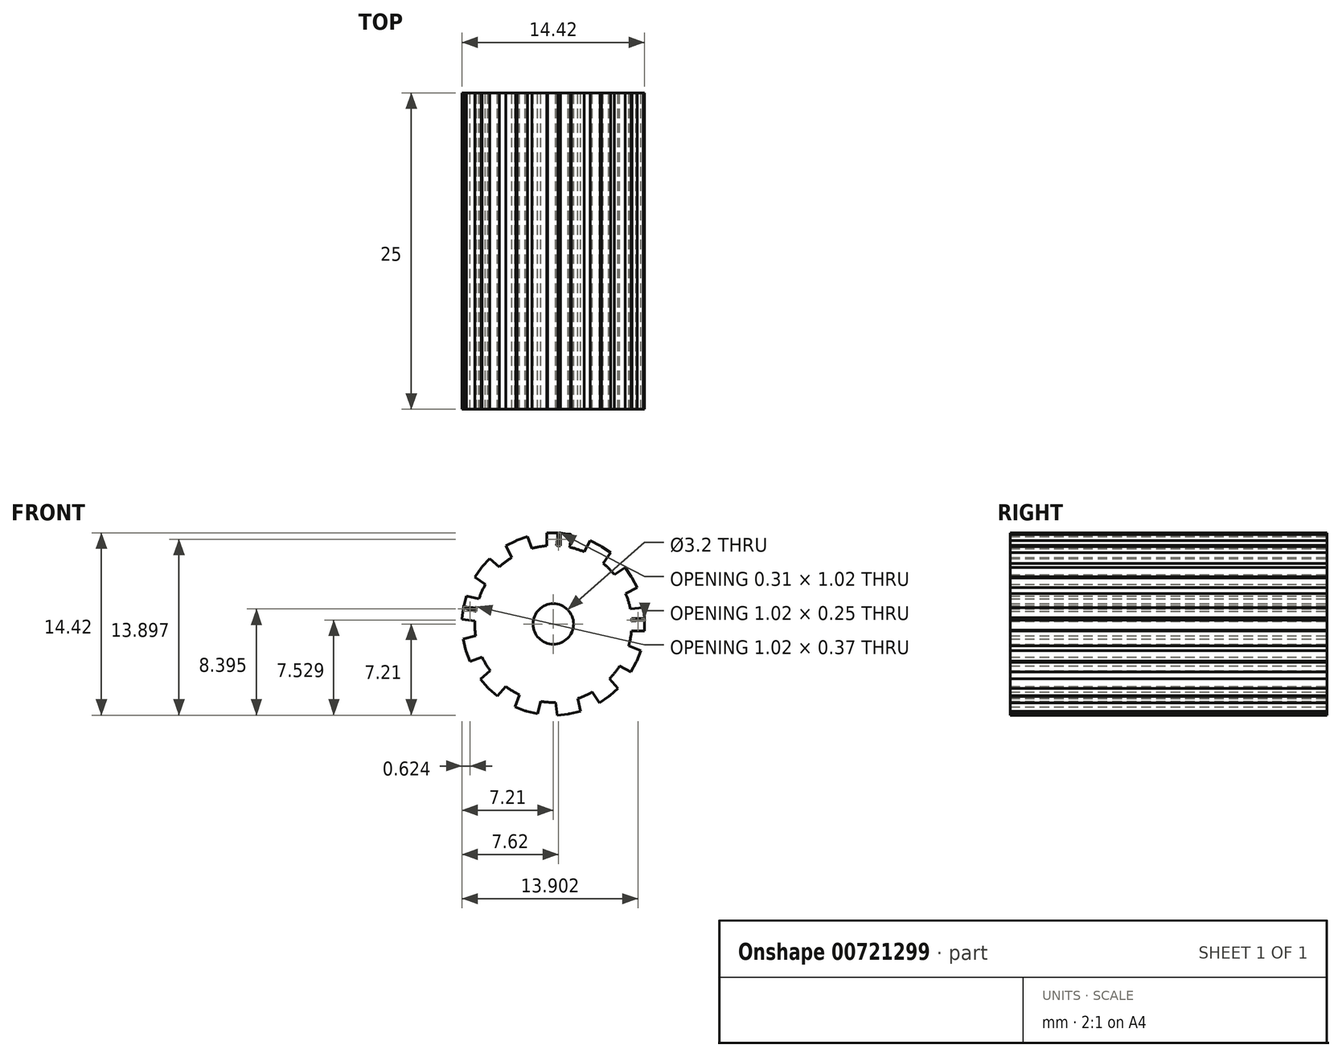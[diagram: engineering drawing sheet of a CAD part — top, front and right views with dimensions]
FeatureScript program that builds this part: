
annotation { "Feature Type Name" : "Feature", "Feature Type Description" : "" }
export const myFeature = defineFeature(function(context is Context, id is Id, definition is map)
    precondition{}
    {
        {
            var Q0;
            Q0=qCreatedBy(makeId("Front.planeOp"),FACE);
            var sketch = newSketch(context, id + "F0", { "sketchPlane" : qUnion([Q0])});
            skCircle(sketch, "E0", {"center": v(0, 0) * mm, "radius": 6.2 * mm});
            skCircle(sketch, "E1", {"center": v(0, 0) * mm, "radius": 4.5 * mm});
            skLineSegment(sketch, "E2", {"start": v(-0.5, 7.2) * mm, "end": v(0.5, 7.2) * mm});
            skLineSegment(sketch, "E3", {"start": v(-0.5, 7.2) * mm, "end": v(-0.5, 6.18) * mm});
            skLineSegment(sketch, "E4", {"start": v(0.5, 7.2) * mm, "end": v(0.5, 6.18) * mm});
            skPoint(sketch, "E5.end.orphan", {"position": v(0, 7.2) * mm});
            skPoint(sketch, "E5.start.orphan", {"position": v(0, 6.2) * mm});
            skLineSegment(sketch, "E6", {"start": v(7.2, 0.5) * mm, "end": v(7.2, -0.5) * mm});
            skLineSegment(sketch, "E7", {"start": v(7.2, 0.5) * mm, "end": v(6.18, 0.5) * mm});
            skLineSegment(sketch, "E8", {"start": v(7.2, -0.5) * mm, "end": v(6.18, -0.5) * mm});
            skPoint(sketch, "E9.end.orphan", {"position": v(7.2, 0) * mm});
            skPoint(sketch, "E9.start.orphan", {"position": v(6.2, 0) * mm});
            skLineSegment(sketch, "E10.1.0", {"start": v(-7.09, 1.37) * mm, "end": v(-6.07, 1.25) * mm});
            skLineSegment(sketch, "E10.1.1", {"start": v(-7.2, 0.38) * mm, "end": v(-6.2, 0.25) * mm});
            skPoint(sketch, "E10.1.2", {"position": v(-7.15, 0.87) * mm});
            skLineSegment(sketch, "E10.1.3", {"start": v(-7.2, 0.38) * mm, "end": v(-7.09, 1.37) * mm});
            skLineSegment(sketch, "E10.1.4", {"start": v(0.38, 7.2) * mm, "end": v(0.25, 6.2) * mm});
            skLineSegment(sketch, "E10.1.5", {"start": v(1.37, 7.09) * mm, "end": v(1.25, 6.07) * mm});
            skLineSegment(sketch, "E10.1.6", {"start": v(0.38, 7.2) * mm, "end": v(1.37, 7.09) * mm});
            skLineSegment(sketch, "E10.2.0", {"start": v(-2.22, -6.87) * mm, "end": v(-1.97, -5.88) * mm});
            skLineSegment(sketch, "E10.2.1", {"start": v(-1.25, -7.1) * mm, "end": v(-1, -6.12) * mm});
            skPoint(sketch, "E10.2.2", {"position": v(-1.73, -6.99) * mm});
            skLineSegment(sketch, "E10.2.3", {"start": v(-1.25, -7.1) * mm, "end": v(-2.22, -6.87) * mm});
            skLineSegment(sketch, "E10.2.4", {"start": v(-7.1, 1.25) * mm, "end": v(-6.12, 1) * mm});
            skLineSegment(sketch, "E10.2.5", {"start": v(-6.87, 2.22) * mm, "end": v(-5.88, 1.97) * mm});
            skLineSegment(sketch, "E10.2.6", {"start": v(-7.1, 1.25) * mm, "end": v(-6.87, 2.22) * mm});
            skLineSegment(sketch, "E10.3.0", {"start": v(6.55, -3.03) * mm, "end": v(5.6, -2.67) * mm});
            skLineSegment(sketch, "E10.3.1", {"start": v(6.9, -2.1) * mm, "end": v(5.95, -1.74) * mm});
            skPoint(sketch, "E10.3.2", {"position": v(6.73, -2.57) * mm});
            skLineSegment(sketch, "E10.3.3", {"start": v(6.9, -2.1) * mm, "end": v(6.55, -3.03) * mm});
            skLineSegment(sketch, "E10.3.4", {"start": v(-2.1, -6.9) * mm, "end": v(-1.74, -5.95) * mm});
            skLineSegment(sketch, "E10.3.5", {"start": v(-3.03, -6.55) * mm, "end": v(-2.67, -5.6) * mm});
            skLineSegment(sketch, "E10.3.6", {"start": v(-2.1, -6.9) * mm, "end": v(-3.03, -6.55) * mm});
            skLineSegment(sketch, "E10.4.0", {"start": v(3.8, 6.13) * mm, "end": v(3.33, 5.23) * mm});
            skLineSegment(sketch, "E10.4.1", {"start": v(2.92, 6.6) * mm, "end": v(2.45, 5.7) * mm});
            skPoint(sketch, "E10.4.2", {"position": v(3.36, 6.37) * mm});
            skLineSegment(sketch, "E10.4.3", {"start": v(2.92, 6.6) * mm, "end": v(3.8, 6.13) * mm});
            skLineSegment(sketch, "E10.4.4", {"start": v(6.6, -2.92) * mm, "end": v(5.7, -2.45) * mm});
            skLineSegment(sketch, "E10.4.5", {"start": v(6.13, -3.8) * mm, "end": v(5.23, -3.33) * mm});
            skLineSegment(sketch, "E10.4.6", {"start": v(6.6, -2.92) * mm, "end": v(6.13, -3.8) * mm});
            skLineSegment(sketch, "E10.5.0", {"start": v(-5.63, 4.52) * mm, "end": v(-4.79, 3.94) * mm});
            skLineSegment(sketch, "E10.5.1", {"start": v(-6.2, 3.7) * mm, "end": v(-5.36, 3.12) * mm});
            skPoint(sketch, "E10.5.2", {"position": v(-5.91, 4.11) * mm});
            skLineSegment(sketch, "E10.5.3", {"start": v(-6.2, 3.7) * mm, "end": v(-5.63, 4.52) * mm});
            skLineSegment(sketch, "E10.5.4", {"start": v(3.7, 6.2) * mm, "end": v(3.12, 5.36) * mm});
            skLineSegment(sketch, "E10.5.5", {"start": v(4.52, 5.63) * mm, "end": v(3.94, 4.79) * mm});
            skLineSegment(sketch, "E10.5.6", {"start": v(3.7, 6.2) * mm, "end": v(4.52, 5.63) * mm});
            skLineSegment(sketch, "E10.6.0", {"start": v(-5.17, -5.04) * mm, "end": v(-4.5, -4.27) * mm});
            skLineSegment(sketch, "E10.6.1", {"start": v(-4.42, -5.7) * mm, "end": v(-3.75, -4.94) * mm});
            skPoint(sketch, "E10.6.2", {"position": v(-4.8, -5.37) * mm});
            skLineSegment(sketch, "E10.6.3", {"start": v(-4.42, -5.7) * mm, "end": v(-5.17, -5.04) * mm});
            skLineSegment(sketch, "E10.6.4", {"start": v(-5.7, 4.42) * mm, "end": v(-4.94, 3.75) * mm});
            skLineSegment(sketch, "E10.6.5", {"start": v(-5.04, 5.17) * mm, "end": v(-4.27, 4.5) * mm});
            skLineSegment(sketch, "E10.6.6", {"start": v(-5.7, 4.42) * mm, "end": v(-5.04, 5.17) * mm});
            skLineSegment(sketch, "E10.7.0", {"start": v(4.37, -5.74) * mm, "end": v(3.7, -4.98) * mm});
            skLineSegment(sketch, "E10.7.1", {"start": v(5.12, -5.08) * mm, "end": v(4.45, -4.32) * mm});
            skPoint(sketch, "E10.7.2", {"position": v(4.75, -5.41) * mm});
            skLineSegment(sketch, "E10.7.3", {"start": v(5.12, -5.08) * mm, "end": v(4.37, -5.74) * mm});
            skLineSegment(sketch, "E10.7.4", {"start": v(-5.08, -5.12) * mm, "end": v(-4.32, -4.45) * mm});
            skLineSegment(sketch, "E10.7.5", {"start": v(-5.74, -4.37) * mm, "end": v(-4.98, -3.7) * mm});
            skLineSegment(sketch, "E10.7.6", {"start": v(-5.08, -5.12) * mm, "end": v(-5.74, -4.37) * mm});
            skLineSegment(sketch, "E10.anchor2", {"start": v(0, 0) * mm, "end": v(-6.06, 1.3) * mm, "construction": true});
            skLineSegment(sketch, "E11.2.8.0", {"start": v(6.23, 3.64) * mm, "end": v(5.39, 3.07) * mm});
            skLineSegment(sketch, "E11.3.8.0", {"start": v(5.67, 4.47) * mm, "end": v(4.82, 3.9) * mm});
            skPoint(sketch, "E11.6.8.0", {"position": v(5.95, 4.06) * mm});
            skLineSegment(sketch, "E11.7.8.0", {"start": v(5.67, 4.47) * mm, "end": v(6.23, 3.64) * mm});
            skLineSegment(sketch, "E11.10.8.0", {"start": v(4.47, -5.67) * mm, "end": v(3.9, -4.82) * mm});
            skLineSegment(sketch, "E11.13.8.0", {"start": v(3.64, -6.23) * mm, "end": v(3.07, -5.39) * mm});
            skLineSegment(sketch, "E11.16.8.0", {"start": v(4.47, -5.67) * mm, "end": v(3.64, -6.23) * mm});
            skLineSegment(sketch, "E11.2.9.0", {"start": v(-2.86, 6.63) * mm, "end": v(-2.4, 5.72) * mm});
            skLineSegment(sketch, "E11.3.9.0", {"start": v(-3.75, 6.17) * mm, "end": v(-3.28, 5.26) * mm});
            skPoint(sketch, "E11.6.9.0", {"position": v(-3.3, 6.4) * mm});
            skLineSegment(sketch, "E11.7.9.0", {"start": v(-3.75, 6.17) * mm, "end": v(-2.86, 6.63) * mm});
            skLineSegment(sketch, "E11.10.9.0", {"start": v(6.17, 3.75) * mm, "end": v(5.26, 3.28) * mm});
            skLineSegment(sketch, "E11.13.9.0", {"start": v(6.63, 2.86) * mm, "end": v(5.72, 2.4) * mm});
            skLineSegment(sketch, "E11.16.9.0", {"start": v(6.17, 3.75) * mm, "end": v(6.63, 2.86) * mm});
            skLineSegment(sketch, "E11.2.10.0", {"start": v(-6.92, -2.04) * mm, "end": v(-5.97, -1.68) * mm});
            skLineSegment(sketch, "E11.3.10.0", {"start": v(-6.58, -2.97) * mm, "end": v(-5.62, -2.62) * mm});
            skPoint(sketch, "E11.6.10.0", {"position": v(-6.75, -2.5) * mm});
            skLineSegment(sketch, "E11.7.10.0", {"start": v(-6.58, -2.97) * mm, "end": v(-6.92, -2.04) * mm});
            skLineSegment(sketch, "E11.10.10.0", {"start": v(-2.97, 6.58) * mm, "end": v(-2.62, 5.62) * mm});
            skLineSegment(sketch, "E11.13.10.0", {"start": v(-2.04, 6.92) * mm, "end": v(-1.68, 5.97) * mm});
            skLineSegment(sketch, "E11.16.10.0", {"start": v(-2.97, 6.58) * mm, "end": v(-2.04, 6.92) * mm});
            skLineSegment(sketch, "E11.2.11.0", {"start": v(1.18, -7.12) * mm, "end": v(0.95, -6.13) * mm});
            skLineSegment(sketch, "E11.3.11.0", {"start": v(2.15, -6.89) * mm, "end": v(1.92, -5.9) * mm});
            skPoint(sketch, "E11.6.11.0", {"position": v(1.67, -7) * mm});
            skLineSegment(sketch, "E11.7.11.0", {"start": v(2.15, -6.89) * mm, "end": v(1.18, -7.12) * mm});
            skLineSegment(sketch, "E11.10.11.0", {"start": v(-6.89, -2.15) * mm, "end": v(-5.9, -1.92) * mm});
            skLineSegment(sketch, "E11.13.11.0", {"start": v(-7.12, -1.18) * mm, "end": v(-6.13, -0.95) * mm});
            skLineSegment(sketch, "E11.16.11.0", {"start": v(-6.89, -2.15) * mm, "end": v(-7.12, -1.18) * mm});
            skLineSegment(sketch, "E12.2.12.0", {"start": v(7.21, 0.3) * mm, "end": v(6.2, 0.2) * mm});
            skLineSegment(sketch, "E12.3.12.0", {"start": v(7.1, 1.3) * mm, "end": v(6.08, 1.19) * mm});
            skPoint(sketch, "E12.6.12.0", {"position": v(7.15, 0.8) * mm});
            skLineSegment(sketch, "E12.7.12.0", {"start": v(7.1, 1.3) * mm, "end": v(7.21, 0.3) * mm});
            skLineSegment(sketch, "E12.10.12.0", {"start": v(1.3, -7.1) * mm, "end": v(1.19, -6.08) * mm});
            skLineSegment(sketch, "E12.13.12.0", {"start": v(0.3, -7.21) * mm, "end": v(0.2, -6.2) * mm});
            skLineSegment(sketch, "E12.16.12.0", {"start": v(1.3, -7.1) * mm, "end": v(0.3, -7.21) * mm});
            skLineSegment(sketch, "E12.2.13.0", {"start": v(0.57, 7.2) * mm, "end": v(0.56, 6.17) * mm});
            skLineSegment(sketch, "E12.3.13.0", {"start": v(-0.43, 7.2) * mm, "end": v(-0.44, 6.18) * mm});
            skPoint(sketch, "E12.6.13.0", {"position": v(0.07, 7.2) * mm});
            skLineSegment(sketch, "E12.7.13.0", {"start": v(-0.43, 7.2) * mm, "end": v(0.57, 7.2) * mm});
            skLineSegment(sketch, "E12.10.13.0", {"start": v(7.2, 0.43) * mm, "end": v(6.18, 0.44) * mm});
            skLineSegment(sketch, "E12.13.13.0", {"start": v(7.2, -0.57) * mm, "end": v(6.17, -0.56) * mm});
            skLineSegment(sketch, "E12.16.13.0", {"start": v(7.2, 0.43) * mm, "end": v(7.2, -0.57) * mm});
            skLineSegment(sketch, "E12.2.14.0", {"start": v(-7.07, 1.44) * mm, "end": v(-6.06, 1.3) * mm});
            skLineSegment(sketch, "E12.3.14.0", {"start": v(-7.2, 0.44) * mm, "end": v(-6.2, 0.31) * mm});
            skPoint(sketch, "E12.6.14.0", {"position": v(-7.14, 0.94) * mm});
            skLineSegment(sketch, "E12.7.14.0", {"start": v(-7.2, 0.44) * mm, "end": v(-7.07, 1.44) * mm});
            skLineSegment(sketch, "E12.10.14.0", {"start": v(0.44, 7.2) * mm, "end": v(0.31, 6.2) * mm});
            skLineSegment(sketch, "E12.13.14.0", {"start": v(1.44, 7.07) * mm, "end": v(1.3, 6.06) * mm});
            skLineSegment(sketch, "E12.16.14.0", {"start": v(0.44, 7.2) * mm, "end": v(1.44, 7.07) * mm});
            skCircle(sketch, "E13", {"center": v(0, 0) * mm, "radius": 2.77 * mm});
            skCircle(sketch, "E14", {"center": v(0, 0) * mm, "radius": 1.6 * mm});
            skSolve(sketch);
        }
        {
            var Q0;
            Q0 = qSketchRegion(id + "F0", true);
            var Q1;
            Q1=makeQuery(id+"F0.imprint","IMPRINT",FACE,{"disambiguationData":[TD([[makeQuery(id+"F0.imprint","IMPRINT",EDGE,{"derivedFrom":sQuery(id+"F0.wireOp",EDGE,"E1")}),1.0]])]});
            var Q2;
            Q2=makeQuery(id+"F0.imprint","IMPRINT",FACE,{"disambiguationData":[TD([[makeQuery(id+"F0.imprint","IMPRINT",EDGE,{"derivedFrom":sQuery(id+"F0.wireOp",EDGE,"E13")}),1.0]])]});
            extrude(context, id + "F1", {"entities" : qUnion([Q0, Q1, Q2]), "depth" : 25 * mm, "offsetDistance" : 25 * mm});
        }
    });
